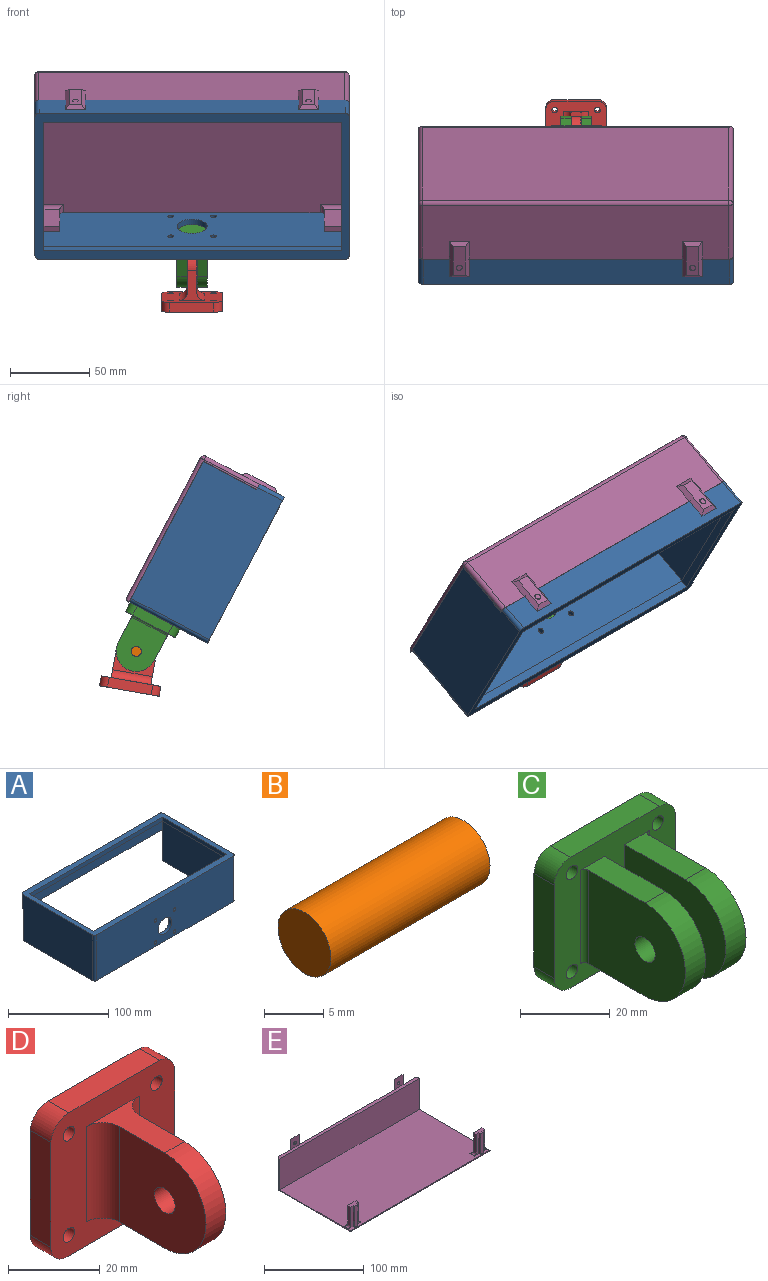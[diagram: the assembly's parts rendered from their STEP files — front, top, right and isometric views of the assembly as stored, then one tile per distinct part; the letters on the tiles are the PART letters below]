
ASSEMBLY  parts=5 mates=5
PART A: 39 faces, bbox 198.1x106x55.9 mm
  f0: cylinder r=1.78mm len=3.56mm, axis (0,-1,0), area 21.3mm2, adj f9,f34
  f1: cylinder r=1.78mm len=3.56mm, axis (0,-1,0), area 21.3mm2, adj f9,f33
  f2: cylinder r=9.53mm len=19.05mm, axis (0,1,0), area 228mm2, adj f11,f14
  f3: cylinder r=1.78mm len=3.81mm, axis (0,-1,0), area 42.6mm2, adj f11,f14
  f4: cylinder r=1.78mm len=3.81mm, axis (0,-1,0), area 42.6mm2, adj f11,f14
  f5: cylinder r=1.78mm len=3.81mm, axis (0,-1,0), area 42.6mm2, adj f11,f14
  f6: cylinder r=1.78mm len=3.81mm, axis (0,-1,0), area 42.6mm2, adj f11,f14
  f7: plane 198.12x3.81mm, normal (0,0,-1), area 752.1mm2, adj f8,f9,f10,f16,f22,f23,f37,f38
  f8: plane 99.06x55.88mm, normal (1,0,0), area 5487.1mm2, adj f7,f12,f22,f24,f35,f38
  f9: plane 193.04x17.78mm, normal (0,1,0), area 3412.4mm2, adj f0,f1,f7,f12,f37,f38
  f10: plane 99.06x55.88mm, normal (-1,0,0), area 5487.1mm2, adj f7,f12,f23,f24,f36,f37
  f11: plane 193.04x55.88mm, normal (0,-1,0), area 10462.3mm2, adj f2,f3,f4,f5,f6,f12,f24,f35
  f12: plane 198.12x104.14mm, normal (0,0,1), area 3439.6mm2, adj f8,f9,f10,f11,f18,f19,f20,f21
  f13: plane 96.52x50.8mm, normal (1,0,0), area 4903.2mm2, adj f14,f16,f17,f23,f24
  f14: plane 193.04x50.8mm, normal (0,1,0), area 9223.6mm2, adj f2,f3,f4,f5,f6,f13,f15,f17
  f15: plane 96.52x50.8mm, normal (-1,0,0), area 4903.2mm2, adj f14,f16,f17,f22,f24
  f16: plane 193.04x12.7mm, normal (0,-1,0), area 2451.6mm2, adj f7,f13,f15,f17
  f17: plane 193.04x96.52mm, normal (0,0,-1), area 1445.2mm2, adj f13,f14,f15,f16,f18,f19,f20,f21
  f18: plane 91.44x5.08mm, normal (1,0,0), area 464.5mm2, adj f12,f17,f19,f21
  f19: plane 187.96x5.08mm, normal (0,1,0), area 954.8mm2, adj f12,f17,f18,f20
  f20: plane 91.44x5.08mm, normal (-1,0,0), area 464.5mm2, adj f12,f17,f19,f21
  f21: plane 187.96x5.08mm, normal (0,-1,0), area 954.8mm2, adj f12,f17,f18,f20
  f22: plane 38.1x2.54mm, normal (0,1,0), area 96.8mm2, adj f7,f8,f15,f24
  f23: plane 38.1x2.54mm, normal (0,1,0), area 96.8mm2, adj f7,f10,f13,f24
  f24: plane 198.12x100.33mm, normal (0,0,-1), area 1216.6mm2, adj f8,f10,f11,f13,f14,f15,f22,f23
  f25: plane 25.4x2.54mm, normal (-1,0,0), area 64.5mm2, adj f14,f24,f26,f28
  f26: plane 5.08x2.54mm, normal (0,0,-1), area 12.9mm2, adj f14,f25,f27,f28
  f27: plane 25.4x2.54mm, normal (1,0,0), area 64.5mm2, adj f14,f24,f26,f28
  f28: plane 25.4x5.08mm, normal (0,1,0), area 129mm2, adj f24,f25,f26,f27
  f29: plane 25.4x2.54mm, normal (-1,0,0), area 64.5mm2, adj f14,f24,f30,f32
  f30: plane 5.08x2.54mm, normal (0,0,-1), area 12.9mm2, adj f14,f29,f31,f32
  f31: plane 25.4x2.54mm, normal (1,0,0), area 64.5mm2, adj f14,f24,f30,f32
  f32: plane 25.4x5.08mm, normal (0,1,0), area 129mm2, adj f24,f29,f30,f31
  f33: plane 3.56x3.56mm, normal (0,1,0), area 9.9mm2, adj f1
  f34: plane 3.56x3.56mm, normal (0,1,0), area 9.9mm2, adj f0
  f35: cylinder r=2.54mm len=55.88mm, axis (0,0,-1), area 223mm2, adj f8,f11,f12,f24
  f36: cylinder r=2.54mm len=55.88mm, axis (0,0,-1), area 223mm2, adj f10,f11,f12,f24
  f37: cylinder r=2.54mm len=17.78mm, axis (0,0,-1), area 70.9mm2, adj f7,f9,f10,f12
  f38: cylinder r=2.54mm len=17.78mm, axis (0,0,-1), area 70.9mm2, adj f7,f8,f9,f12
PART B: 3 faces, bbox 19.1x6.4x6.4 mm
  f0: cylinder r=3.17mm len=19.05mm, axis (-1,0,0), area 380mm2, adj f1,f2
  f1: plane 6.35x6.35mm, normal (1,0,0), area 31.7mm2, adj f0
  f2: plane 6.35x6.35mm, normal (-1,0,0), area 31.7mm2, adj f0
PART C: 28 faces, bbox 38.1x38.1x35.6 mm
  f0: plane 38.1x35.56mm, normal (0,-1,0), area 905.9mm2, adj f1,f2,f3,f4,f5,f6,f7,f8
  f1: plane 25.4x6.35mm, normal (-1,0,0), area 161.3mm2, adj f0,f11,f24,f27
  f2: plane 27.94x6.35mm, normal (0,0,-1), area 177.4mm2, adj f0,f11,f24,f25
  f3: plane 25.4x6.35mm, normal (1,0,0), area 161.3mm2, adj f0,f11,f25,f26
  f4: plane 31.75x25.4mm, normal (-1,0,0), area 705.6mm2, adj f0,f15,f17,f21,f22
  f5: cylinder r=1.78mm len=6.35mm, axis (0,1,0), area 70.9mm2, adj f0,f11
  f6: cylinder r=1.78mm len=6.35mm, axis (0,1,0), area 70.9mm2, adj f0,f11
  f7: cylinder r=1.78mm len=6.35mm, axis (0,1,0), area 70.9mm2, adj f0,f11
  f8: cylinder r=1.78mm len=6.35mm, axis (0,1,0), area 70.9mm2, adj f0,f11
  f9: plane 31.75x25.4mm, normal (1,0,0), area 705.6mm2, adj f0,f12,f14,f20,f23
  f10: plane 27.94x6.35mm, normal (0,0,1), area 177.4mm2, adj f0,f11,f26,f27
  f11: plane 38.1x35.56mm, normal (0,1,0), area 1293mm2, adj f1,f2,f3,f5,f6,f7,f8,f10
  f12: plane 19.05x7.62mm, normal (0,0,1), area 121.3mm2, adj f0,f9,f13,f19,f20
  f13: plane 30.48x25.4mm, normal (-1,0,0), area 673.3mm2, adj f12,f14,f19,f20,f23
  f14: plane 19.05x7.62mm, normal (0,0,-1), area 121.3mm2, adj f0,f9,f13,f19,f20
  f15: plane 19.05x7.62mm, normal (0,0,-1), area 121.3mm2, adj f0,f4,f16,f18,f21
  f16: plane 30.48x25.4mm, normal (1,0,0), area 673.3mm2, adj f15,f17,f18,f21,f22
  f17: plane 19.05x7.62mm, normal (0,0,1), area 121.3mm2, adj f0,f4,f16,f18,f21
  f18: cylinder r=1.27mm len=25.4mm, axis (0,0,-1), area 50.7mm2, adj f0,f15,f16,f17
  f19: cylinder r=1.27mm len=25.4mm, axis (0,0,1), area 50.7mm2, adj f0,f12,f13,f14
  f20: cylinder r=12.7mm len=25.4mm, axis (-1,0,0), area 253.4mm2, adj f9,f12,f13,f14
  f21: cylinder r=12.7mm len=25.4mm, axis (-1,0,0), area 253.4mm2, adj f4,f15,f16,f17
  f22: cylinder r=3.17mm len=6.35mm, axis (1,0,0), area 126.7mm2, adj f4,f16
  f23: cylinder r=3.17mm len=6.35mm, axis (1,0,0), area 126.7mm2, adj f9,f13
  f24: cylinder r=5.08mm len=6.35mm, axis (0,-1,0), area 50.7mm2, adj f0,f1,f2,f11
  f25: cylinder r=5.08mm len=6.35mm, axis (0,1,0), area 50.7mm2, adj f0,f2,f3,f11
  f26: cylinder r=5.08mm len=6.35mm, axis (0,-1,0), area 50.7mm2, adj f0,f3,f10,f11
  f27: cylinder r=5.08mm len=6.35mm, axis (0,1,0), area 50.7mm2, adj f0,f1,f10,f11
PART D: 22 faces, bbox 38.1x38.1x38.1 mm
  f0: plane 27.94x6.35mm, normal (0,0,1), area 177.4mm2, adj f1,f11,f12,f13
  f1: cylinder r=5.59mm len=6.35mm, axis (0,1,0), area 52.6mm2, adj f0,f2,f12,f13
  f2: plane 27.94x6.35mm, normal (-1,0,0), area 177.4mm2, adj f1,f3,f12,f13
  f3: cylinder r=5.08mm len=6.35mm, axis (0,1,0), area 50.7mm2, adj f2,f4,f12,f13
  f4: plane 27.94x6.35mm, normal (0,0,-1), area 177.4mm2, adj f3,f5,f12,f13
  f5: cylinder r=5.08mm len=6.35mm, axis (0,1,0), area 50.7mm2, adj f4,f6,f12,f13
  f6: plane 27.94x6.35mm, normal (1,0,0), area 177.4mm2, adj f5,f11,f12,f13
  f7: cylinder r=1.78mm len=6.35mm, axis (0,1,0), area 70.9mm2, adj f12,f13
  f8: cylinder r=1.78mm len=6.35mm, axis (0,1,0), area 70.9mm2, adj f12,f13
  f9: cylinder r=1.78mm len=6.35mm, axis (0,1,0), area 70.9mm2, adj f12,f13
  f10: cylinder r=1.78mm len=6.35mm, axis (0,1,0), area 70.9mm2, adj f12,f13
  f11: cylinder r=5.08mm len=6.35mm, axis (0,1,0), area 47.8mm2, adj f0,f6,f12,f13
  f12: plane 38.11x38.1mm, normal (0,-1,0), area 976.3mm2, adj f0,f1,f2,f3,f4,f5,f6,f7
  f13: plane 38.11x38.1mm, normal (0,1,0), area 1389.2mm2, adj f0,f1,f2,f3,f4,f5,f6,f7
  f14: plane 26.67x25.4mm, normal (-1,0,0), area 576.5mm2, adj f15,f17,f18,f19,f20
  f15: plane 19.05x16.26mm, normal (0,0,-1), area 127.2mm2, adj f12,f14,f16,f18,f20,f21
  f16: plane 26.67x25.4mm, normal (1,0,0), area 576.5mm2, adj f15,f17,f18,f19,f21
  f17: plane 19.05x16.26mm, normal (0,0,1), area 127.2mm2, adj f12,f14,f16,f18,f20,f21
  f18: cylinder r=12.7mm len=25.4mm, axis (-1,0,0), area 243.2mm2, adj f14,f15,f16,f17
  f19: cylinder r=3.17mm len=6.35mm, axis (-1,0,0), area 121.6mm2, adj f14,f16
  f20: cylinder r=5.08mm len=25.4mm, axis (0,0,1), area 202.7mm2, adj f12,f14,f15,f17
  f21: cylinder r=5.08mm len=25.4mm, axis (0,0,-1), area 202.7mm2, adj f12,f15,f16,f17
PART E: 55 faces, bbox 198.1x106.7x53.3 mm
  f0: cylinder r=1.91mm len=3.81mm, axis (0,-1,0), area 25.8mm2, adj f49,f50
  f1: cylinder r=1.91mm len=3.81mm, axis (0,-1,0), area 25.8mm2, adj f42,f43
  f2: plane 193.04x38.1mm, normal (0,1,0), area 7032.2mm2, adj f32,f35,f36,f40,f44,f45,f46,f52
  f3: plane 198.12x100.33mm, normal (0,0,1), area 19639.3mm2, adj f8,f9,f10,f11,f12,f16,f17,f18
  f4: plane 38.1x1.27mm, normal (1,0,0), area 48.4mm2, adj f31,f32,f34,f35
  f5: plane 38.1x1.27mm, normal (-1,0,0), area 48.4mm2, adj f31,f32,f36,f37
  f6: plane 193.04x99.06mm, normal (0,0,-1), area 19122.5mm2, adj f33,f34,f37,f40
  f7: plane 22.86x3.81mm, normal (-1,0,0), area 87.1mm2, adj f8,f14,f15,f30
  f8: plane 25.4x6.35mm, normal (0,-1,0), area 98.2mm2, adj f3,f7,f9,f15,f30
  f9: plane 25.4x2.54mm, normal (-1,0,0), area 64.5mm2, adj f3,f8,f10,f15
  f10: plane 25.4x4.32mm, normal (0,-1,0), area 109.7mm2, adj f3,f9,f11,f15
  f11: plane 25.4x2.54mm, normal (1,0,0), area 64.5mm2, adj f3,f10,f12,f15
  f12: plane 25.4x6.35mm, normal (0,-1,0), area 98.2mm2, adj f3,f11,f13,f15,f28
  f13: plane 22.86x3.81mm, normal (1,0,0), area 87.1mm2, adj f12,f14,f15,f28
  f14: plane 22.86x11.94mm, normal (0,1,0), area 272.9mm2, adj f7,f13,f15,f29
  f15: plane 11.94x6.35mm, normal (0,0,1), area 56.5mm2, adj f7,f8,f9,f10,f11,f12,f13,f14
  f16: plane 25.4x2.54mm, normal (-1,0,0), area 64.5mm2, adj f3,f17,f23,f24
  f17: plane 25.4x4.32mm, normal (0,-1,0), area 109.7mm2, adj f3,f16,f18,f24
  f18: plane 25.4x2.54mm, normal (1,0,0), area 64.5mm2, adj f3,f17,f19,f24
  f19: plane 25.4x6.35mm, normal (0,-1,0), area 98.2mm2, adj f3,f18,f20,f24,f27
  f20: plane 22.86x3.81mm, normal (1,0,0), area 87.1mm2, adj f19,f21,f24,f27
  f21: plane 22.86x11.94mm, normal (0,1,0), area 272.9mm2, adj f20,f22,f24,f26
  f22: plane 22.86x3.81mm, normal (-1,0,0), area 87.1mm2, adj f21,f23,f24,f25
  f23: plane 25.4x6.35mm, normal (0,-1,0), area 98.2mm2, adj f3,f16,f22,f24,f25
  f24: plane 11.94x6.35mm, normal (0,0,1), area 56.5mm2, adj f16,f17,f18,f19,f20,f21,f22,f23
  f25: cylinder r=2.54mm len=6.35mm, axis (0,-1,0), area 18.9mm2, adj f3,f22,f23,f26
  f26: cylinder r=2.54mm len=17.02mm, axis (-1,0,0), area 55mm2, adj f3,f21,f25,f27
  f27: cylinder r=2.54mm len=6.35mm, axis (0,1,0), area 18.9mm2, adj f3,f19,f20,f26
  f28: cylinder r=2.54mm len=6.35mm, axis (0,1,0), area 18.9mm2, adj f3,f12,f13,f29
  f29: cylinder r=2.54mm len=17.02mm, axis (-1,0,0), area 55mm2, adj f3,f14,f28,f30
  f30: cylinder r=2.54mm len=6.35mm, axis (0,-1,0), area 18.9mm2, adj f3,f7,f8,f29
  f31: plane 198.12x38.1mm, normal (0,-1,0), area 7548.4mm2, adj f3,f4,f5,f32
  f32: plane 198.12x3.81mm, normal (0,0,1), area 752.1mm2, adj f2,f4,f5,f31,f35,f36,f42,f49
  f33: cylinder r=2.54mm len=198.12mm, axis (1,0,0), area 783.1mm2, adj f3,f6,f34,f37
  f34: cylinder r=2.54mm len=101.6mm, axis (0,1,0), area 401.7mm2, adj f3,f4,f6,f33,f38
  f35: cylinder r=2.54mm len=38.1mm, axis (0,0,-1), area 152mm2, adj f2,f4,f32,f38
  f36: cylinder r=2.54mm len=38.1mm, axis (0,0,-1), area 152mm2, adj f2,f5,f32,f39
  f37: cylinder r=2.54mm len=101.6mm, axis (0,-1,0), area 401.7mm2, adj f3,f5,f6,f33,f39
  f38: sphere r=2.54mm, area 10.1mm2, adj f34,f35,f40
  f39: sphere r=2.54mm, area 10.1mm2, adj f36,f37,f40
  f40: cylinder r=2.54mm len=193.04mm, axis (-1,0,0), area 770.2mm2, adj f2,f6,f38,f39
  f41: plane 20.32x7.62mm, normal (0,1,0), area 154.8mm2, adj f44,f45,f46,f47
  f42: plane 12.7x12.7mm, normal (0,-1,0), area 149.9mm2, adj f1,f32,f45,f46,f47
  f43: plane 3.81x3.81mm, normal (0,-1,0), area 11.4mm2, adj f1
  f44: plane 12.7x2.54mm, normal (0,0.71,-0.71), area 36.5mm2, adj f2,f41,f45,f46
  f45: plane 25.4x2.54mm, normal (-0.71,0.71,0), area 82.1mm2, adj f2,f41,f42,f44,f47
  f46: plane 25.4x2.54mm, normal (0.71,0.71,0), area 82.1mm2, adj f2,f41,f42,f44,f47
  f47: plane 12.7x2.54mm, normal (0,0.71,0.71), area 36.5mm2, adj f41,f42,f45,f46
  f48: plane 20.32x7.62mm, normal (0,1,0), area 154.8mm2, adj f51,f52,f53,f54
  f49: plane 12.7x12.7mm, normal (0,-1,0), area 149.9mm2, adj f0,f32,f51,f52,f53
  f50: plane 3.81x3.81mm, normal (0,-1,0), area 11.4mm2, adj f0
  f51: plane 12.7x2.54mm, normal (0,0.71,0.71), area 36.5mm2, adj f48,f49,f52,f53
  f52: plane 25.4x2.54mm, normal (-0.71,0.71,0), area 82.1mm2, adj f2,f48,f49,f51,f54
  f53: plane 25.4x2.54mm, normal (0.71,0.71,0), area 82.1mm2, adj f2,f48,f49,f51,f54
  f54: plane 12.7x2.54mm, normal (0,0.71,-0.71), area 36.5mm2, adj f2,f48,f52,f53
PLACE A rot(axis=(1,0,0),117.8deg) t=(0.13,72.94,-86.71)mm
PLACE B t=(-9.41,173.93,-146.15)mm
PLACE C rot(axis=(1,0,0),117.8deg) t=(0.11,114.49,-123.68)mm
PLACE D rot(axis=(0,0.77,-0.64),180deg) t=(-43.84,130.74,-171.16)mm
PLACE E rot(axis=(1,0,0),117.8deg) t=(0,109.01,-67.99)mm
MATE revolute D.f19 <-> B.f0  axis (1,0,0) through (0.11,126.33,-146.15)mm
MATE parallel A.f11 <-> C.f11  axis (0,0.47,-0.88) through (0.13,105.94,-128.18)mm
MATE fastened C.f6 <-> A.f6  axis (0,-0.47,0.88) through (-13.35,126.42,-117.39)mm
MATE fastened A.f1 <-> E.f1  axis (0,-0.47,0.88) through (-73.53,43.28,-41.33)mm
MATE revolute B.f0 <-> C.f20  axis (1,0,0) through (9.64,126.33,-146.15)mm
